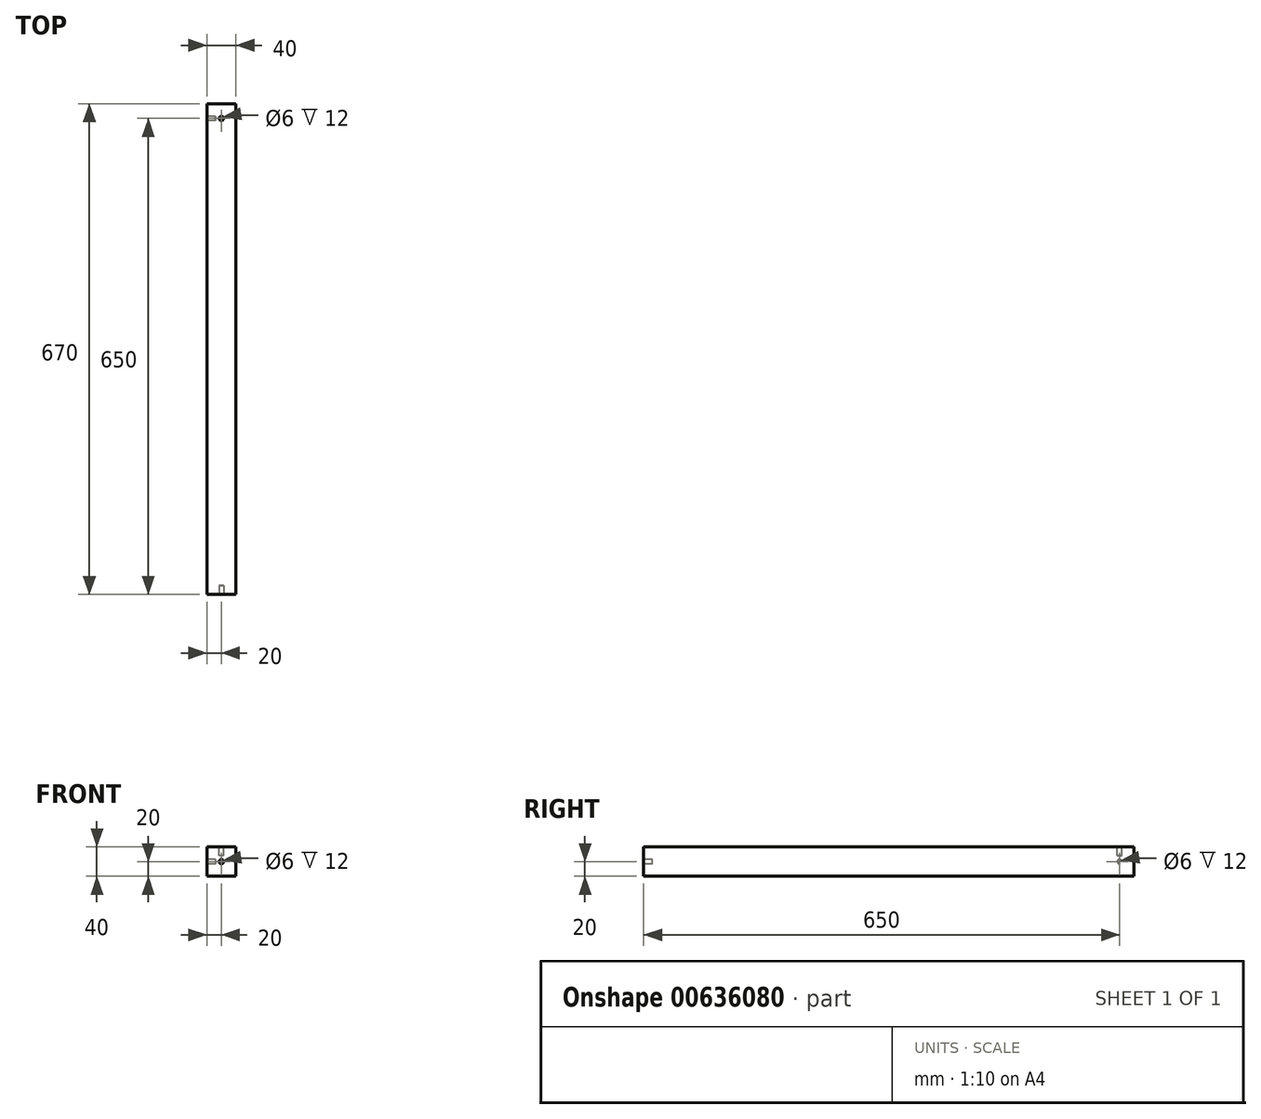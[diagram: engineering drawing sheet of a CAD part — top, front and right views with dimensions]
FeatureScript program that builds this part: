
annotation { "Feature Type Name" : "Feature", "Feature Type Description" : "" }
export const myFeature = defineFeature(function(context is Context, id is Id, definition is map)
    precondition{}
    {
        {
            var Q0;
            Q0=qCreatedBy(makeId("Front.planeOp"),FACE);
            var sketch = newSketch(context, id + "F0", { "sketchPlane" : qUnion([Q0])});
            skLineSegment(sketch, "E0.bottom", {"start": v(0, 0) * mm, "end": v(40, 0) * mm});
            skLineSegment(sketch, "E0.top", {"start": v(0, 40) * mm, "end": v(40, 40) * mm});
            skLineSegment(sketch, "E0.left", {"start": v(0, 0) * mm, "end": v(0, 40) * mm});
            skLineSegment(sketch, "E0.right", {"start": v(40, 0) * mm, "end": v(40, 40) * mm});
            skSolve(sketch);
        }
        {
            var Q0;
            Q0 = qSketchRegion(id + "F0", true);
            extrude(context, id + "F1", {"entities" : qUnion([Q0]), "depth" : 670 * mm, "offsetDistance" : 25 * mm});
        }
        {
            var Q0;
            Q0=makeQuery(id+"F1.opExtrude","CAP_FACE",FACE,{"disambiguationData":[OSD([sQuery(id+"F0.wireOp",EDGE,"E0.bottom"),sQuery(id+"F0.wireOp",EDGE,"E0.top"),sQuery(id+"F0.wireOp",EDGE,"E0.left"),sQuery(id+"F0.wireOp",EDGE,"E0.right")])],"isStart":false});
            var sketch = newSketch(context, id + "F2", { "sketchPlane" : qUnion([Q0])});
            skCircle(sketch, "E1", {"center": v(20, 20) * mm, "radius": 3 * mm});
            skSolve(sketch);
        }
        {
            var Q0;
            Q0 = qSketchRegion(id + "F2", true);
            extrude(context, id + "F3", {"entities" : qUnion([Q0]), "operationType" : NewBodyOperationType.REMOVE, "oppositeDirection" : true, "depth" : 12 * mm, "offsetDistance" : 25 * mm});
        }
        {
            var Q0;
            Q0=makeQuery(id+"F1.opExtrude","SWEPT_FACE",FACE,{"disambiguationData":[OSD([sQuery(id+"F0.wireOp",EDGE,"E0.left")])]});
            var sketch = newSketch(context, id + "F4", { "sketchPlane" : qUnion([Q0])});
            skCircle(sketch, "E2", {"center": v(20, 20) * mm, "radius": 3 * mm});
            skSolve(sketch);
        }
        {
            var Q0;
            Q0 = qSketchRegion(id + "F4", true);
            extrude(context, id + "F5", {"entities" : qUnion([Q0]), "operationType" : NewBodyOperationType.REMOVE, "oppositeDirection" : true, "depth" : 12 * mm, "offsetDistance" : 25 * mm});
        }
        {
            var Q0;
            Q0=makeQuery(id+"F1.opExtrude","SWEPT_FACE",FACE,{"disambiguationData":[OSD([sQuery(id+"F0.wireOp",EDGE,"E0.top")])]});
            var sketch = newSketch(context, id + "F6", { "sketchPlane" : qUnion([Q0])});
            skCircle(sketch, "E3", {"center": v(20, -20) * mm, "radius": 3 * mm});
            skSolve(sketch);
        }
        {
            var Q0;
            Q0 = qSketchRegion(id + "F6", true);
            extrude(context, id + "F7", {"entities" : qUnion([Q0]), "operationType" : NewBodyOperationType.REMOVE, "oppositeDirection" : true, "depth" : 12 * mm, "offsetDistance" : 25 * mm});
        }
    });
